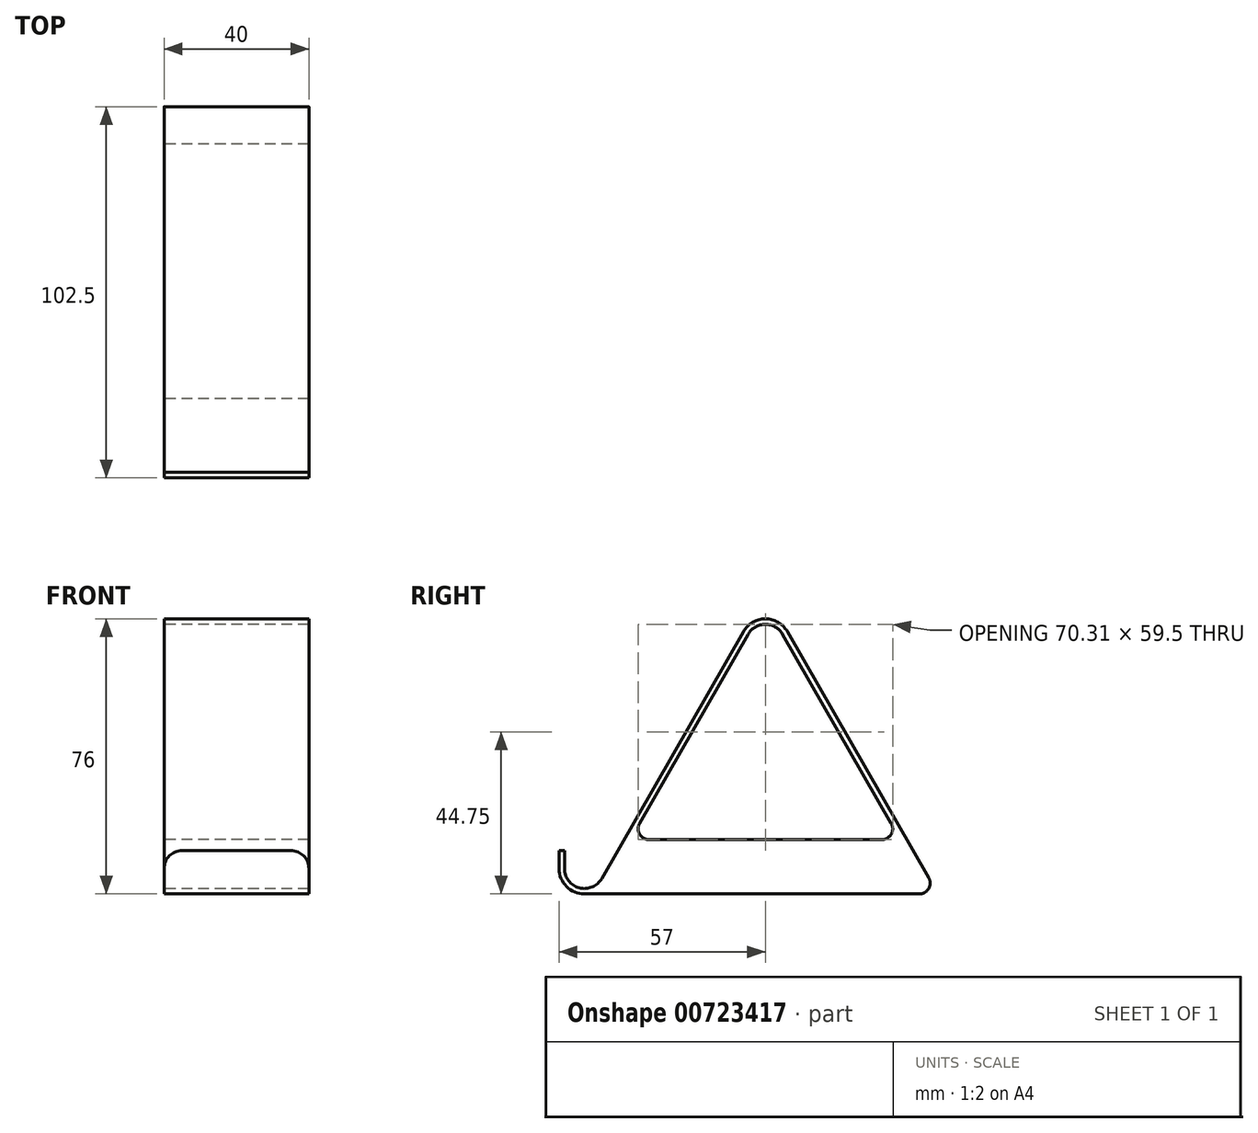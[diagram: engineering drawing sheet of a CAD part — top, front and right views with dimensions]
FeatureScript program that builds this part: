
annotation { "Feature Type Name" : "Feature", "Feature Type Description" : "" }
export const myFeature = defineFeature(function(context is Context, id is Id, definition is map)
    precondition{}
    {
        {
            var Q0;
            Q0=qCreatedBy(makeId("Right.planeOp"),FACE);
            var sketch = newSketch(context, id + "F0", { "sketchPlane" : qUnion([Q0])});
            skArc(sketch, "E0", {"start": v(-7, 0) * mm, "mid": v(-4.95, -4.95) * mm, "end": v(0, -7) * mm});
            skArc(sketch, "E1", {"start": v(54.77, 64.74) * mm, "mid": v(50, 67.5) * mm, "end": v(45.23, 64.74) * mm});
            skLineSegment(sketch, "E2", {"start": v(15.24, 12.5) * mm, "end": v(45.23, 64.74) * mm});
            skLineSegment(sketch, "E3", {"start": v(50, 62) * mm, "end": v(50, -40.59) * mm, "construction": true});
            skLineSegment(sketch, "E4.MirrorCS", {"start": v(84.76, 12.5) * mm, "end": v(54.77, 64.74) * mm});
            skLineSegment(sketch, "E5", {"start": v(0, -7) * mm, "end": v(92.5, -7) * mm, "construction": true});
            skPoint(sketch, "E6.orphan", {"position": v(93.93, -3.48) * mm});
            skLineSegment(sketch, "E7", {"start": v(-7, 0) * mm, "end": v(-7, 5) * mm});
            skLineSegment(sketch, "E8.0", {"start": v(-5.5, 0) * mm, "end": v(-5.5, 5) * mm});
            skLineSegment(sketch, "E8.1", {"start": v(95.1, -2.5) * mm, "end": v(56.07, 65.48) * mm});
            skArc(sketch, "E8.2", {"start": v(56.07, 65.48) * mm, "mid": v(50, 69) * mm, "end": v(43.93, 65.48) * mm});
            skLineSegment(sketch, "E8.3", {"start": v(4.77, -2.74) * mm, "end": v(43.93, 65.48) * mm});
            skArc(sketch, "E8.4", {"start": v(-5.5, 0) * mm, "mid": v(-1.42, -5.31) * mm, "end": v(4.77, -2.74) * mm});
            skLineSegment(sketch, "E9", {"start": v(-5.5, 5) * mm, "end": v(-7, 5) * mm});
            skLineSegment(sketch, "E10", {"start": v(0, -7) * mm, "end": v(97.68, -7) * mm});
            skLineSegment(sketch, "E11.0", {"start": v(17.84, 8) * mm, "end": v(82.16, 8) * mm});
            skPoint(sketch, "E12.orphan", {"position": v(6.07, -3.48) * mm});
            skPoint(sketch, "E13.visualSharp", {"position": v(12.66, 8) * mm});
            skArc(sketch, "E13.filletArc", {"start": v(15.24, 12.5) * mm, "mid": v(15.25, 9.5) * mm, "end": v(17.84, 8) * mm});
            skPoint(sketch, "E14.visualSharp", {"position": v(87.34, 8) * mm});
            skArc(sketch, "E14.filletArc", {"start": v(82.16, 8) * mm, "mid": v(84.75, 9.5) * mm, "end": v(84.76, 12.5) * mm});
            skArc(sketch, "E15.filletArc", {"start": v(92.5, -7) * mm, "mid": v(95.1, -5.5) * mm, "end": v(95.1, -2.5) * mm});
            skSolve(sketch);
        }
        {
            var Q0;
            {var subQ0=sQuery(id+"F0.wireOp",EDGE,"E0");Q0=makeQuery(id+"F0.imprint","IMPRINT",FACE,{"disambiguationData":[TD([[makeQuery(id+"F0.imprint","IMPRINT",EDGE,{"derivedFrom":subQ0}),1.0]])]});}
            extrude(context, id + "F1", {"entities" : qUnion([Q0]), "depth" : 40 * mm, "offsetDistance" : 25 * mm});
        }
        {
            var Q0;
            Q0=makeQuery(id+"F1.opExtrude","CAP_EDGE",EDGE,{"disambiguationData":[OSD([sQuery(id+"F0.wireOp",EDGE,"E9")])],"isStart":false});
            var Q1;
            Q1=makeQuery(id+"F1.opExtrude","CAP_EDGE",EDGE,{"disambiguationData":[OSD([sQuery(id+"F0.wireOp",EDGE,"E9")])],"isStart":true});
            fillet(context, id + "F2", {"entities" : qUnion([Q0, Q1]), "radius" : 5 * mm, "tangentPropagation" : true, "allowEdgeOverflow" : false});
        }
    });
